# Revit family: Rough Cut Lumber-Side
name_source: partatom
category: Detail Items
revit_build: Autodesk Revit Architecture 2012 (Build: 20110210_1515)
units: mm (PartAtom-declared; Revit-internal decimal feet)

## types (48) — shared parameters

## per-type parameters (varying)
| type | Depth | Keynote | Width |
| 1x3R | 0' - 3" | 06 01 10.A1 | 0' - 1" |
| 1x4R | 0' - 4" | 06 01 10.A2 | 0' - 1" |
| 1x6R | 0' - 6" | 06 01 10.A3 | 0' - 1" |
| 1x8R | 0' - 8" | 06 01 10.A4 | 0' - 1" |
| 1x10R | 0' - 10" | 06 01 10.A5 | 0' - 1" |
| 1x12R | 1' - 0" | 06 01 10.A6 | 0' - 1" |
| 2x3R | 0' - 3" | 06 01 10.B1 | 0' - 2" |
| 2x4R | 0' - 4" | 06 01 10.B2 | 0' - 2" |
| 2x6R | 0' - 6" | 06 01 10.B3 | 0' - 2" |
| 2x8R | 0' - 8" | 06 01 10.B4 | 0' - 2" |
| 2x10R | 0' - 10" | 06 01 10.B5 | 0' - 2" |
| 2x12R | 1' - 0" | 06 01 10.B6 | 0' - 2" |
| 2x14R | 1' - 2" | 06 01 10.B7 | 0' - 2" |
| 3x4R | 0' - 4" | 06 01 10.C1 | 0' - 3" |
| 3x6R | 0' - 6" | 06 01 10.C2 | 0' - 3" |
| 3x8R | 0' - 8" | 06 01 10.C3 | 0' - 3" |
| 3x10R | 0' - 10" | 06 01 10.C4 | 0' - 3" |
| 3x12R | 1' - 0" | 06 01 10.C5 | 0' - 3" |
| 3x14R | 1' - 2" | 06 01 10.C6 | 0' - 3" |
| 3x16R | 1' - 4" | 06 01 10.C7 | 0' - 3" |
| 4x4R | 0' - 4" | 06 01 10.D1 | 0' - 4" |
| 4x6R | 0' - 6" | 06 01 10.D2 | 0' - 4" |
| 4x8R | 0' - 8" | 06 01 10.D3 | 0' - 4" |
| 4x10R | 0' - 10" | 06 01 10.D4 | 0' - 4" |
| 4x12R | 1' - 0" | 06 01 10.D5 | 0' - 4" |
| 4x14R | 1' - 2" | 06 01 10.D6 | 0' - 4" |
| 4x16R | 1' - 4" | 06 01 10.D7 | 0' - 4" |
| 6x6R | 0' - 6" | 06 01 10.E1 | 0' - 6" |
| 6x8R | 0' - 8" | 06 01 10.E2 | 0' - 6" |
| 6x10R | 0' - 10" | 06 01 10.E3 | 0' - 6" |
| 6x12R | 1' - 0" | 06 01 10.E4 | 0' - 6" |
| 6x14R | 1' - 2" | 06 01 10.E5 | 0' - 6" |
| 6x16R | 1' - 4" | 06 01 10.E6 | 0' - 6" |
| 8x8R | 0' - 8" | 06 01 10.F1 | 0' - 8" |
| 8x10R | 0' - 10" | 06 01 10.F2 | 0' - 8" |
| 8x12R | 1' - 0" | 06 01 10.F3 | 0' - 8" |
| 8x14R | 1' - 2" | 06 01 10.F4 | 0' - 8" |
| 8x16R | 1' - 4" | 06 01 10.F5 | 0' - 8" |
| 10x10R | 0' - 10" | 06 01 10.G1 | 0' - 10" |
| 10x12R | 1' - 0" | 06 01 10.G2 | 0' - 10" |
| 10x14R | 1' - 2" | 06 01 10.G3 | 0' - 10" |
| 10x16R | 1' - 4" | 06 01 10.G4 | 0' - 10" |
| 12x12R | 1' - 0" | 06 01 10.H1 | 1' - 0" |
| 12x14R | 1' - 2" | 06 01 10.H2 | 1' - 0" |
| 12x16R | 1' - 4" | 06 01 10.H3 | 1' - 0" |
| 14x14R | 1' - 2" | 06 01 10.I1 | 1' - 2" |
| 14x16R | 1' - 4" | 06 01 10.I2 | 1' - 2" |
| 16x16R | 1' - 4" | 06 01 10.J1 | 1' - 4" |

## geometry (parser evidence)
native form markers: Sweep x1
no freeform markers — native parametric forms only
